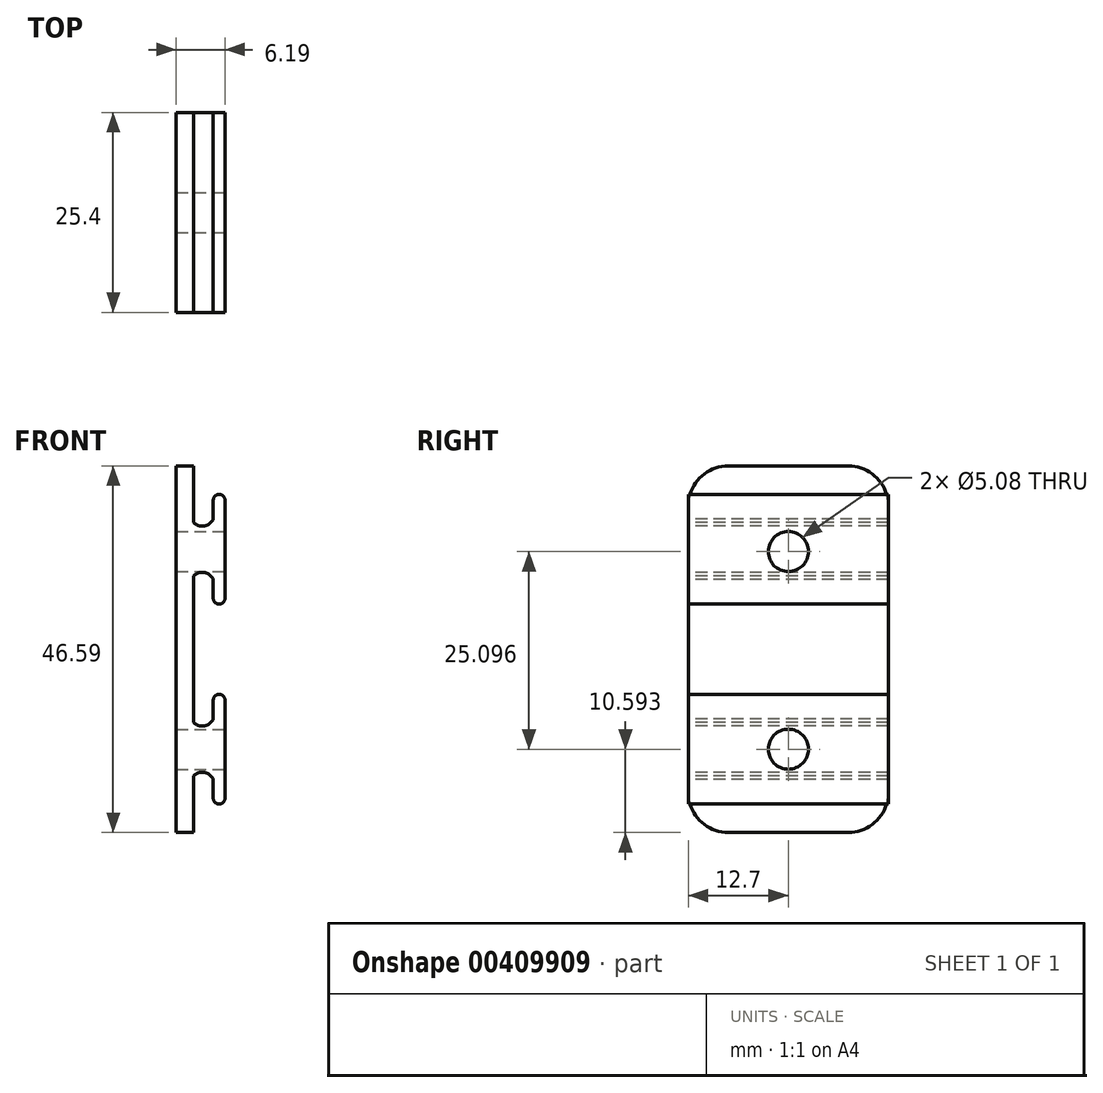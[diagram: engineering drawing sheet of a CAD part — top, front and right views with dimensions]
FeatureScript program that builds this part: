
annotation { "Feature Type Name" : "Feature", "Feature Type Description" : "" }
export const myFeature = defineFeature(function(context is Context, id is Id, definition is map)
    precondition{}
    {
        {
            var Q0;
            Q0=qCreatedBy(makeId("Front.planeOp"),FACE);
            var sketch = newSketch(context, id + "F0", { "sketchPlane" : qUnion([Q0])});
            skLineSegment(sketch, "E0", {"start": v(-12.43, 10.9) * mm, "end": v(-12.43, 4.65) * mm});
            skLineSegment(sketch, "E1", {"start": v(-11.21, 7.74) * mm, "end": v(-10, 7.74) * mm, "construction": true});
            skLineSegment(sketch, "E2", {"start": v(-13.33, 3.54) * mm, "end": v(-12.05, 3.54) * mm, "construction": true});
            skLineSegment(sketch, "E3.MirrorCS", {"start": v(-11.21, -7.13) * mm, "end": v(-10, -7.13) * mm, "construction": true});
            skLineSegment(sketch, "E4.MirrorCS", {"start": v(-12.43, -10.29) * mm, "end": v(-12.43, -4.04) * mm});
            skLineSegment(sketch, "E5.MirrorCS", {"start": v(-13.33, -2.94) * mm, "end": v(-12.05, -2.94) * mm, "construction": true});
            skLineSegment(sketch, "E6.MirrorCS", {"start": v(-11.21, -32.53) * mm, "end": v(-10, -32.53) * mm, "construction": true});
            skLineSegment(sketch, "E7.MirrorCS", {"start": v(-13.33, -28.34) * mm, "end": v(-12.05, -28.34) * mm, "construction": true});
            skLineSegment(sketch, "E8.MirrorCS", {"start": v(-13.33, -21.86) * mm, "end": v(-12.05, -21.86) * mm, "construction": true});
            skLineSegment(sketch, "E9.MirrorCS", {"start": v(-11.21, -17.66) * mm, "end": v(-10, -17.66) * mm, "construction": true});
            skLineSegment(sketch, "E10.MirrorCS", {"start": v(-12.43, -14.5) * mm, "end": v(-12.43, -20.75) * mm});
            skLineSegment(sketch, "E11.MirrorCS", {"start": v(-12.43, -35.69) * mm, "end": v(-12.43, -29.44) * mm});
            skLineSegment(sketch, "E12", {"start": v(-12.43, 10.9) * mm, "end": v(-14.64, 10.9) * mm});
            skLineSegment(sketch, "E13", {"start": v(-14.64, 10.9) * mm, "end": v(-14.64, -10.29) * mm});
            skLineSegment(sketch, "E14", {"start": v(-14.64, -10.29) * mm, "end": v(-14.64, -35.69) * mm});
            skLineSegment(sketch, "E15", {"start": v(-12.43, -35.69) * mm, "end": v(-14.64, -35.69) * mm});
            skPoint(sketch, "E16.orphan", {"position": v(-14.64, -36.23) * mm});
            skLineSegment(sketch, "E17", {"start": v(-12.43, -10.29) * mm, "end": v(-12.43, -14.5) * mm});
            skArc(sketch, "E18", {"start": v(-12.43, 3.69) * mm, "mid": v(-11.07, 3.26) * mm, "end": v(-9.94, 4.13) * mm});
            skLineSegment(sketch, "E19", {"start": v(-9.94, 4.13) * mm, "end": v(-9.94, 6.52) * mm});
            skLineSegment(sketch, "E20", {"start": v(-8.45, 6.52) * mm, "end": v(-8.45, -5.9) * mm});
            skArc(sketch, "E21", {"start": v(-8.45, 6.52) * mm, "mid": v(-9.2, 7.26) * mm, "end": v(-9.94, 6.52) * mm});
            skLineSegment(sketch, "E22", {"start": v(-12.43, 4.65) * mm, "end": v(-12.43, 3.69) * mm});
            skArc(sketch, "E23", {"start": v(-12.43, -21.71) * mm, "mid": v(-11.07, -22.14) * mm, "end": v(-9.94, -21.27) * mm});
            skLineSegment(sketch, "E24", {"start": v(-9.94, -21.27) * mm, "end": v(-9.94, -18.88) * mm});
            skArc(sketch, "E25", {"start": v(-8.45, -18.88) * mm, "mid": v(-9.2, -18.14) * mm, "end": v(-9.94, -18.88) * mm});
            skLineSegment(sketch, "E26", {"start": v(-12.43, -20.75) * mm, "end": v(-12.43, -21.71) * mm});
            skLineSegment(sketch, "E27.MirrorCS", {"start": v(-12.43, -4.04) * mm, "end": v(-12.43, -3.08) * mm});
            skArc(sketch, "E28.MirrorCS", {"start": v(-12.43, -3.08) * mm, "mid": v(-11.07, -2.65) * mm, "end": v(-9.94, -3.52) * mm});
            skLineSegment(sketch, "E29.MirrorCS", {"start": v(-9.94, -3.52) * mm, "end": v(-9.94, -5.9) * mm});
            skArc(sketch, "E30.MirrorCS", {"start": v(-8.45, -5.9) * mm, "mid": v(-9.2, -6.65) * mm, "end": v(-9.94, -5.9) * mm});
            skArc(sketch, "E31.MirrorCS", {"start": v(-12.43, -28.48) * mm, "mid": v(-11.07, -28.05) * mm, "end": v(-9.94, -28.92) * mm});
            skArc(sketch, "E32.MirrorCS", {"start": v(-8.45, -31.3) * mm, "mid": v(-9.2, -32.05) * mm, "end": v(-9.94, -31.3) * mm});
            skLineSegment(sketch, "E33.MirrorCS", {"start": v(-12.43, -29.44) * mm, "end": v(-12.43, -28.48) * mm});
            skLineSegment(sketch, "E34.MirrorCS", {"start": v(-9.94, -28.92) * mm, "end": v(-9.94, -31.3) * mm});
            skLineSegment(sketch, "E35.trimOffspring", {"start": v(-8.45, -18.88) * mm, "end": v(-8.45, -31.3) * mm});
            skSolve(sketch);
        }
        {
            var Q0;
            Q0=makeQuery(id+"F0.imprint","IMPRINT",FACE,{"disambiguationData":[TD([[makeQuery(id+"F0.imprint","IMPRINT",EDGE,{"derivedFrom":sQuery(id+"F0.wireOp",EDGE,"E0")}),-1.0]])]});
            extrude(context, id + "F1", {"entities" : qUnion([Q0]), "oppositeDirection" : true, "depth" : 25.4 * mm});
        }
        {
            var Q0;
            Q0=makeQuery(id+"F1.opExtrude","CAP_EDGE",EDGE,{"disambiguationData":[OSD([sQuery(id+"F0.wireOp",EDGE,"E15")])],"isStart":false});
            var Q1;
            Q1=makeQuery(id+"F1.opExtrude","CAP_EDGE",EDGE,{"disambiguationData":[OSD([sQuery(id+"F0.wireOp",EDGE,"E15")])],"isStart":true});
            var Q2;
            Q2=makeQuery(id+"F1.opExtrude","CAP_EDGE",EDGE,{"disambiguationData":[OSD([sQuery(id+"F0.wireOp",EDGE,"E12")])],"isStart":false});
            var Q3;
            Q3=makeQuery(id+"F1.opExtrude","CAP_EDGE",EDGE,{"disambiguationData":[OSD([sQuery(id+"F0.wireOp",EDGE,"E12")])],"isStart":true});
            fillet(context, id + "F2", {"entities" : qUnion([Q0, Q1, Q2, Q3]), "radius" : 5.08 * mm, "tangentPropagation" : true, "allowEdgeOverflow" : false});
        }
        {
            var Q0;
            Q0=makeQuery(id+"F1.opExtrude","SWEPT_FACE",FACE,{"disambiguationData":[OSD([sQuery(id+"F0.wireOp",EDGE,"E20")])]});
            var sketch = newSketch(context, id + "F3", { "sketchPlane" : qUnion([Q0])});
            skCircle(sketch, "E36", {"center": v(12.7, 0) * mm, "radius": 2.54 * mm});
            skSolve(sketch);
        }
        {
            var Q0;
            Q0=makeQuery(id+"F3.imprint","IMPRINT",FACE,{"disambiguationData":[TD([[makeQuery(id+"F3.imprint","IMPRINT",EDGE,{"derivedFrom":sQuery(id+"F3.wireOp",EDGE,"E36")}),1.0]])]});
            extrude(context, id + "F4", {"entities" : qUnion([Q0]), "operationType" : NewBodyOperationType.REMOVE, "oppositeDirection" : true, "depth" : 25.4 * mm});
        }
        {
            var Q0;
            Q0=makeQuery(id+"F1.opExtrude","SWEPT_FACE",FACE,{"disambiguationData":[OSD([sQuery(id+"F0.wireOp",EDGE,"E35.trimOffspring")])]});
            var sketch = newSketch(context, id + "F5", { "sketchPlane" : qUnion([Q0])});
            skCircle(sketch, "E37", {"center": v(12.7, -25.1) * mm, "radius": 2.54 * mm});
            skSolve(sketch);
        }
        {
            var Q0;
            Q0=makeQuery(id+"F5.imprint","IMPRINT",FACE,{"disambiguationData":[TD([[makeQuery(id+"F5.imprint","IMPRINT",EDGE,{"derivedFrom":sQuery(id+"F5.wireOp",EDGE,"E37")}),1.0]])]});
            extrude(context, id + "F6", {"entities" : qUnion([Q0]), "operationType" : NewBodyOperationType.REMOVE, "oppositeDirection" : true, "depth" : 25.4 * mm});
        }
    });
